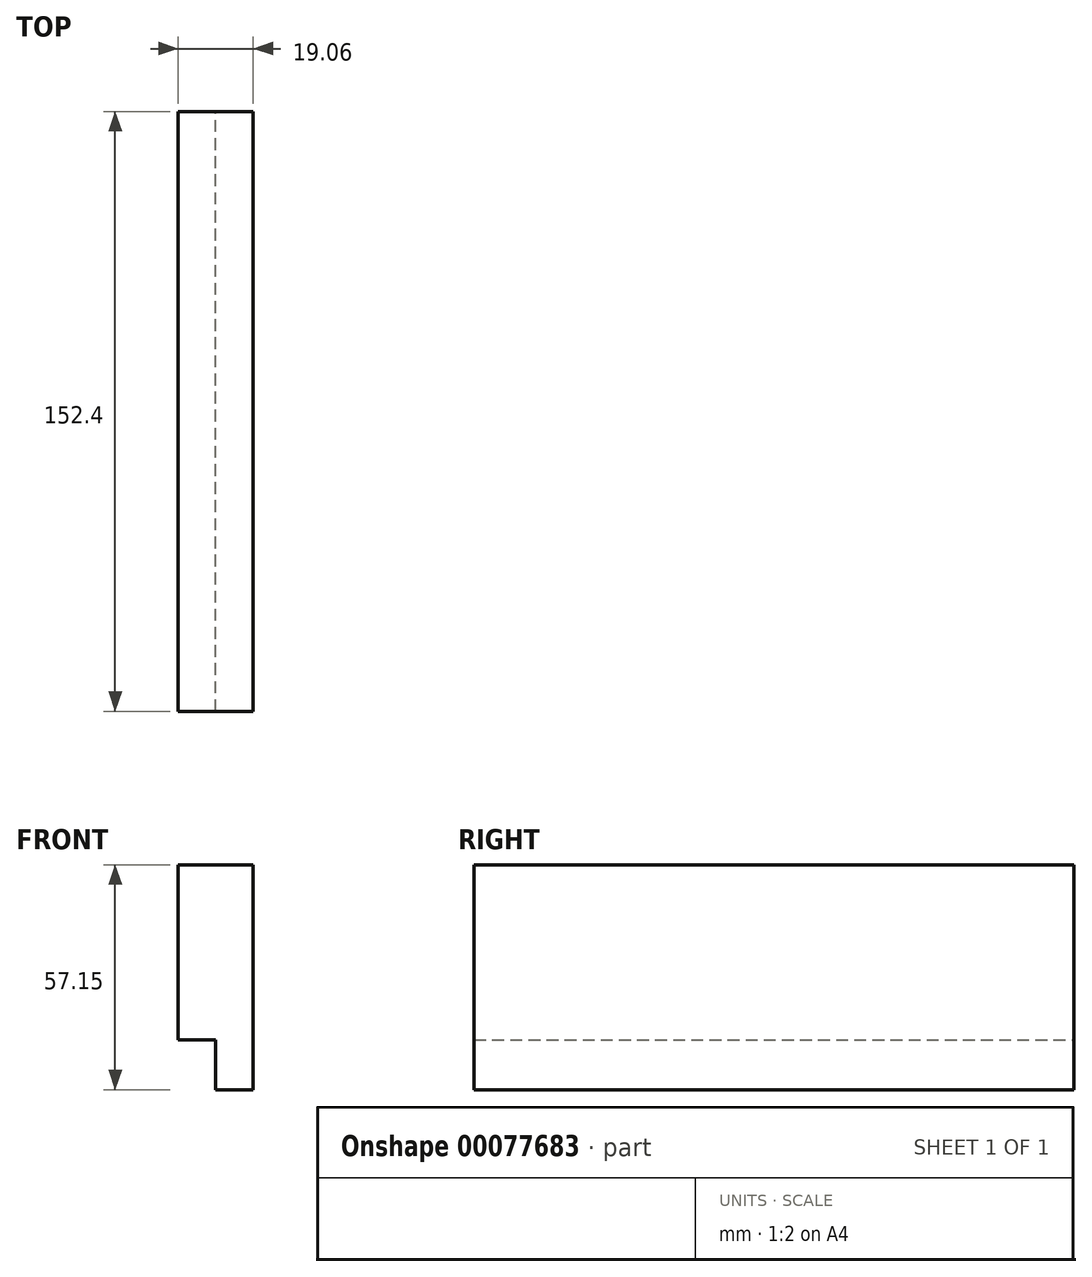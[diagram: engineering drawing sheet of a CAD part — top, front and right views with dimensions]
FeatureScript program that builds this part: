
annotation { "Feature Type Name" : "Feature", "Feature Type Description" : "" }
export const myFeature = defineFeature(function(context is Context, id is Id, definition is map)
    precondition{}
    {
        {
            var Q0;
            Q0=qCreatedBy(makeId("Front.planeOp"),FACE);
            var sketch = newSketch(context, id + "F0", { "sketchPlane" : qUnion([Q0])});
            skLineSegment(sketch, "E0", {"start": v(9.53, -15.88) * mm, "end": v(9.53, -28.58) * mm});
            skLineSegment(sketch, "E1", {"start": v(9.53, -28.58) * mm, "end": v(0, -28.58) * mm});
            skLineSegment(sketch, "E2", {"start": v(0, -28.58) * mm, "end": v(0, -15.88) * mm});
            skLineSegment(sketch, "E3", {"start": v(0, -15.88) * mm, "end": v(-9.53, -15.88) * mm});
            skLineSegment(sketch, "E4", {"start": v(-9.53, -15.88) * mm, "end": v(-9.53, 28.58) * mm});
            skLineSegment(sketch, "E5", {"start": v(9.53, -15.88) * mm, "end": v(9.53, 28.58) * mm});
            skLineSegment(sketch, "E6", {"start": v(-9.53, -15.88) * mm, "end": v(0, -15.88) * mm});
            skLineSegment(sketch, "E7", {"start": v(-9.53, 28.58) * mm, "end": v(9.53, 28.58) * mm});
            skSolve(sketch);
        }
        {
            var Q0;
            Q0=makeQuery(id+"F0.imprint","IMPRINT",FACE,{"disambiguationData":[TD([[makeQuery(id+"F0.imprint","IMPRINT",EDGE,{"derivedFrom":sQuery(id+"F0.wireOp",EDGE,"E0")}),-1.0]])]});
            extrude(context, id + "F1", {"entities" : qUnion([Q0]), "depth" : 152.4 * mm});
        }
    });
